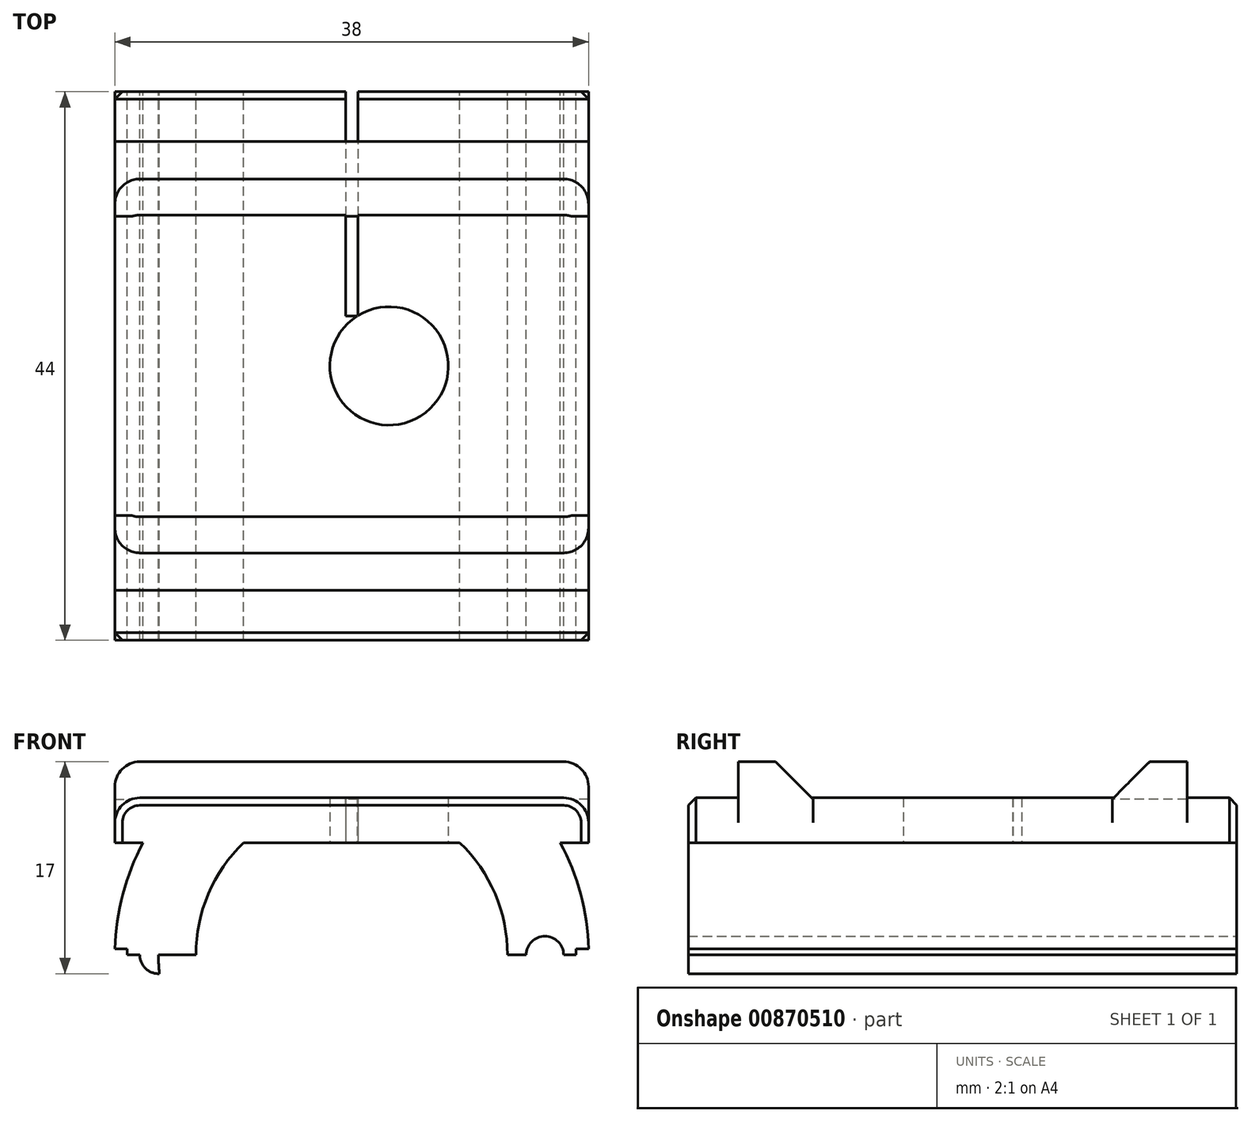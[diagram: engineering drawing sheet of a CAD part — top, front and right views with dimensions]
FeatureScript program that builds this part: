
annotation { "Feature Type Name" : "Feature", "Feature Type Description" : "" }
export const myFeature = defineFeature(function(context is Context, id is Id, definition is map)
    precondition{}
    {
        {
            var Q0;
            Q0=qCreatedBy(makeId("Top.planeOp"),FACE);
            var sketch = newSketch(context, id + "F0", { "sketchPlane" : qUnion([Q0])});
            skLineSegment(sketch, "E0.bottom", {"start": v(9.5, 19) * mm, "end": v(-9.5, 19) * mm});
            skLineSegment(sketch, "E0.top", {"start": v(9.5, -19) * mm, "end": v(-9.5, -19) * mm});
            skLineSegment(sketch, "E0.left", {"start": v(9.5, 19) * mm, "end": v(9.5, -19) * mm});
            skLineSegment(sketch, "E0.right", {"start": v(-9.5, 19) * mm, "end": v(-9.5, -19) * mm});
            skPoint(sketch, "E0.middle", {"position": v(0, 0) * mm});
            skLineSegment(sketch, "E1.bottom", {"start": v(-13.5, 22) * mm, "end": v(13.5, 22) * mm});
            skLineSegment(sketch, "E1.top", {"start": v(-13.5, -22) * mm, "end": v(13.5, -22) * mm});
            skLineSegment(sketch, "E1.left", {"start": v(-13.5, 22) * mm, "end": v(-13.5, -22) * mm});
            skLineSegment(sketch, "E1.right", {"start": v(13.5, 22) * mm, "end": v(13.5, -22) * mm});
            skCircle(sketch, "E2", {"center": v(3, 0) * mm, "radius": 4.75 * mm});
            skLineSegment(sketch, "E3.bottom", {"start": v(-0.5, 4) * mm, "end": v(0.5, 4) * mm});
            skLineSegment(sketch, "E3.top", {"start": v(-0.5, 29) * mm, "end": v(0.5, 29) * mm});
            skLineSegment(sketch, "E3.left", {"start": v(-0.5, 4) * mm, "end": v(-0.5, 29) * mm});
            skLineSegment(sketch, "E3.right", {"start": v(0.5, 4) * mm, "end": v(0.5, 29) * mm});
            skPoint(sketch, "E3.middle", {"position": v(0, 16.5) * mm});
            skPoint(sketch, "E3.middle.positionSnap0", {"position": v(0, 19) * mm});
            skPoint(sketch, "E3.centerSnap0", {"position": v(0, 19) * mm});
            skLineSegment(sketch, "E4.bottom", {"start": v(18.55, 25) * mm, "end": v(-18.55, 25) * mm});
            skLineSegment(sketch, "E4.top", {"start": v(18.55, -25) * mm, "end": v(-18.55, -25) * mm});
            skLineSegment(sketch, "E4.left", {"start": v(18.55, 25) * mm, "end": v(18.55, -25) * mm});
            skLineSegment(sketch, "E4.right", {"start": v(-18.55, 25) * mm, "end": v(-18.55, -25) * mm});
            skSolve(sketch);
        }
        {
            var Q0;
            Q0=qCreatedBy(makeId("Front.planeOp"),FACE);
            var sketch = newSketch(context, id + "F1", { "sketchPlane" : qUnion([Q0])});
            skCircle(sketch, "E5", {"center": v(0, 0) * mm, "radius": 9.5 * mm});
            skLineSegment(sketch, "E6.bottom", {"start": v(9.5, 6) * mm, "end": v(-9.5, 6) * mm});
            skLineSegment(sketch, "E6.top", {"start": v(9.5, -6) * mm, "end": v(-9.5, -6) * mm});
            skLineSegment(sketch, "E6.left", {"start": v(9.5, 6) * mm, "end": v(9.5, -6) * mm});
            skLineSegment(sketch, "E6.right", {"start": v(-9.5, 6) * mm, "end": v(-9.5, -6) * mm});
            skCircle(sketch, "E7", {"center": v(0, 0) * mm, "radius": 12.5 * mm});
            skLineSegment(sketch, "E8.bottom", {"start": v(-15.14, 9) * mm, "end": v(15.14, 9) * mm});
            skLineSegment(sketch, "E8.top", {"start": v(-15.14, -9) * mm, "end": v(15.14, -9) * mm});
            skLineSegment(sketch, "E8.left", {"start": v(-15.14, 9) * mm, "end": v(-15.14, -9) * mm});
            skLineSegment(sketch, "E8.right", {"start": v(15.14, 9) * mm, "end": v(15.14, -9) * mm});
            skLineSegment(sketch, "E9.bottom", {"start": v(-19, 12.6) * mm, "end": v(19, 12.6) * mm});
            skLineSegment(sketch, "E9.top", {"start": v(-19, -12.6) * mm, "end": v(19, -12.6) * mm});
            skLineSegment(sketch, "E9.left", {"start": v(-19, 12.6) * mm, "end": v(-19, -12.6) * mm});
            skLineSegment(sketch, "E9.right", {"start": v(19, 12.6) * mm, "end": v(19, -12.6) * mm});
            skCircle(sketch, "E10", {"center": v(0, 0) * mm, "radius": 15.5 * mm});
            skLineSegment(sketch, "E11", {"start": v(-15.14, 9) * mm, "end": v(-19, 9) * mm});
            skLineSegment(sketch, "E12", {"start": v(15.14, 9) * mm, "end": v(19, 9) * mm});
            skLineSegment(sketch, "E13", {"start": v(-15.14, -9) * mm, "end": v(-19, -9) * mm});
            skLineSegment(sketch, "E14", {"start": v(15.14, -9) * mm, "end": v(19, -9) * mm});
            skCircle(sketch, "E15", {"center": v(0, 0) * mm, "radius": 19 * mm});
            skLineSegment(sketch, "E16", {"start": v(-19, 0) * mm, "end": v(19, 0) * mm});
            skCircle(sketch, "E17", {"center": v(-15.5, 0) * mm, "radius": 1.5 * mm});
            skPoint(sketch, "E17.centerSnap0", {"position": v(-15.14, 0) * mm});
            skCircle(sketch, "E18", {"center": v(15.5, 0) * mm, "radius": 1.5 * mm});
            skLineSegment(sketch, "E19.bottom", {"start": v(-19, 0) * mm, "end": v(-18, 0) * mm});
            skLineSegment(sketch, "E19.top", {"start": v(-19, 0.5) * mm, "end": v(-18, 0.5) * mm});
            skLineSegment(sketch, "E19.left", {"start": v(-19, 0) * mm, "end": v(-19, 0.5) * mm});
            skLineSegment(sketch, "E19.right", {"start": v(-18, 0) * mm, "end": v(-18, 0.5) * mm});
            skLineSegment(sketch, "E20.bottom", {"start": v(19, 0) * mm, "end": v(18, 0) * mm});
            skLineSegment(sketch, "E20.top", {"start": v(19, 0.5) * mm, "end": v(18, 0.5) * mm});
            skLineSegment(sketch, "E20.left", {"start": v(19, 0) * mm, "end": v(19, 0.5) * mm});
            skLineSegment(sketch, "E20.right", {"start": v(18, 0) * mm, "end": v(18, 0.5) * mm});
            skSolve(sketch);
        }
        {
            var Q0;
            {var subQ7=sQuery(id+"F1.wireOp",EDGE,"E16");var subQ9=sQuery(id+"F1.wireOp",EDGE,"E7");var subQ11=makeQuery(id+"F1.imprint","INTERSECT",VERTEX,{"disambiguationData":[OD(0.0)],"derivedFrom":[subQ9,subQ7]});Q0=makeQuery(id+"F1.imprint","IMPRINT",FACE,{"disambiguationData":[TD([[makeQuery(id+"F1.imprint","IMPRINT",EDGE,{"disambiguationData":[TD([[subQ11,-1.0]])],"derivedFrom":subQ9}),-1.0]])]});}
            var Q1;
            {var subQ0=sQuery(id+"F1.wireOp",EDGE,"E8.bottom");var subQ1=sQuery(id+"F1.wireOp",EDGE,"E5");var subQ2=makeQuery(id+"F1.imprint","INTERSECT",VERTEX,{"disambiguationData":[OD(0.0)],"derivedFrom":[subQ1,subQ0]});Q1=makeQuery(id+"F1.imprint","IMPRINT",FACE,{"disambiguationData":[TD([[makeQuery(id+"F1.imprint","IMPRINT",EDGE,{"disambiguationData":[TD([[subQ2,1.0]])],"derivedFrom":subQ1}),-1.0]])]});}
            var Q2;
            {var subQ0=sQuery(id+"F1.wireOp",EDGE,"E10");var subQ1=sQuery(id+"F1.wireOp",EDGE,"E8.bottom");var subQ2=makeQuery(id+"F1.imprint","INTERSECT",VERTEX,{"disambiguationData":[OD(0.0)],"derivedFrom":[subQ1,subQ0]});Q2=makeQuery(id+"F1.imprint","IMPRINT",FACE,{"disambiguationData":[TD([[makeQuery(id+"F1.imprint","IMPRINT",EDGE,{"disambiguationData":[TD([[subQ2,-1.0]])],"derivedFrom":subQ0}),-1.0]])]});}
            var Q3;
            {var subQ1=sQuery(id+"F1.wireOp",EDGE,"E8.bottom");var subQ3=sQuery(id+"F1.wireOp",EDGE,"E10");var subQ4=makeQuery(id+"F1.imprint","INTERSECT",VERTEX,{"disambiguationData":[OD(1.0)],"derivedFrom":[subQ1,subQ3]});Q3=makeQuery(id+"F1.imprint","IMPRINT",FACE,{"disambiguationData":[TD([[makeQuery(id+"F1.imprint","IMPRINT",EDGE,{"disambiguationData":[TD([[subQ4,1.0]])],"derivedFrom":subQ3}),-1.0]])]});}
            var Q4;
            {var subQ0=sQuery(id+"F1.wireOp",EDGE,"E8.bottom");var subQ1=sQuery(id+"F1.wireOp",EDGE,"E7");var subQ2=makeQuery(id+"F1.imprint","INTERSECT",VERTEX,{"disambiguationData":[OD(0.0)],"derivedFrom":[subQ1,subQ0]});Q4=makeQuery(id+"F1.imprint","IMPRINT",FACE,{"disambiguationData":[TD([[makeQuery(id+"F1.imprint","IMPRINT",EDGE,{"disambiguationData":[TD([[subQ2,-1.0]])],"derivedFrom":subQ1}),-1.0]])]});}
            var Q5;
            {var subQ0=sQuery(id+"F1.wireOp",EDGE,"E8.bottom");var subQ1=sQuery(id+"F1.wireOp",EDGE,"E7");var subQ2=makeQuery(id+"F1.imprint","INTERSECT",VERTEX,{"disambiguationData":[OD(0.0)],"derivedFrom":[subQ1,subQ0]});Q5=makeQuery(id+"F1.imprint","IMPRINT",FACE,{"disambiguationData":[TD([[makeQuery(id+"F1.imprint","IMPRINT",EDGE,{"disambiguationData":[TD([[subQ2,-1.0]])],"derivedFrom":subQ1}),-1.0]])]});}
            var Q6;
            {var subQ0=sQuery(id+"F1.wireOp",EDGE,"E10");var subQ1=sQuery(id+"F1.wireOp",EDGE,"E8.left");var subQ2=makeQuery(id+"F1.imprint","INTERSECT",VERTEX,{"disambiguationData":[OD(0.0)],"derivedFrom":[subQ1,subQ0]});Q6=makeQuery(id+"F1.imprint","IMPRINT",FACE,{"disambiguationData":[TD([[makeQuery(id+"F1.imprint","IMPRINT",EDGE,{"disambiguationData":[TD([[subQ2,-1.0]])],"derivedFrom":subQ1}),-1.0]])]});}
            var Q7;
            {var subQ0=sQuery(id+"F1.wireOp",EDGE,"E10");var subQ1=sQuery(id+"F1.wireOp",EDGE,"E8.right");var subQ2=makeQuery(id+"F1.imprint","INTERSECT",VERTEX,{"disambiguationData":[OD(1.0)],"derivedFrom":[subQ1,subQ0]});Q7=makeQuery(id+"F1.imprint","IMPRINT",FACE,{"disambiguationData":[TD([[makeQuery(id+"F1.imprint","IMPRINT",EDGE,{"disambiguationData":[TD([[subQ2,-1.0]])],"derivedFrom":subQ1}),1.0]])]});}
            var Q8;
            {var subQ0=sQuery(id+"F1.wireOp",EDGE,"E15");var subQ1=sQuery(id+"F1.wireOp",EDGE,"E9.bottom");var subQ2=makeQuery(id+"F1.imprint","INTERSECT",VERTEX,{"disambiguationData":[OD(0.0)],"derivedFrom":[subQ1,subQ0]});Q8=makeQuery(id+"F1.imprint","IMPRINT",FACE,{"disambiguationData":[TD([[makeQuery(id+"F1.imprint","IMPRINT",EDGE,{"disambiguationData":[TD([[subQ2,1.0]])],"derivedFrom":subQ1}),-1.0]])]});}
            var Q9;
            {var subQ5=sQuery(id+"F1.wireOp",EDGE,"E10");var subQ7=sQuery(id+"F1.wireOp",EDGE,"E9.bottom");var subQ8=makeQuery(id+"F1.imprint","INTERSECT",VERTEX,{"disambiguationData":[OD(0.0)],"derivedFrom":[subQ7,subQ5]});Q9=makeQuery(id+"F1.imprint","IMPRINT",FACE,{"disambiguationData":[TD([[makeQuery(id+"F1.imprint","IMPRINT",EDGE,{"disambiguationData":[TD([[subQ8,1.0]])],"derivedFrom":subQ7}),-1.0]])]});}
            var Q10;
            {var subQ0=sQuery(id+"F1.wireOp",EDGE,"E15");var subQ7=sQuery(id+"F1.wireOp",EDGE,"E9.bottom");var subQ9=makeQuery(id+"F1.imprint","INTERSECT",VERTEX,{"disambiguationData":[OD(1.0)],"derivedFrom":[subQ7,subQ0]});Q10=makeQuery(id+"F1.imprint","IMPRINT",FACE,{"disambiguationData":[TD([[makeQuery(id+"F1.imprint","IMPRINT",EDGE,{"disambiguationData":[TD([[subQ9,1.0]])],"derivedFrom":subQ7}),-1.0]])]});}
            var Q11;
            {var subQ0=sQuery(id+"F1.wireOp",EDGE,"E9.right");var subQ1=sQuery(id+"F1.wireOp",EDGE,"E9.bottom");var subQ2=makeQuery(id+"F1.imprint","INTERSECT",VERTEX,{"derivedFrom":[subQ1,subQ0]});Q11=makeQuery(id+"F1.imprint","IMPRINT",FACE,{"disambiguationData":[TD([[makeQuery(id+"F1.imprint","IMPRINT",EDGE,{"disambiguationData":[TD([[subQ2,1.0]])],"derivedFrom":subQ1}),-1.0]])]});}
            var Q12;
            {var subQ11=sQuery(id+"F1.wireOp",EDGE,"E19.right");Q12=makeQuery(id+"F1.imprint","IMPRINT",FACE,{"disambiguationData":[TD([[makeQuery(id+"F1.imprint","IMPRINT",EDGE,{"derivedFrom":subQ11}),-1.0]])]});}
            var Q13;
            {var subQ11=sQuery(id+"F1.wireOp",EDGE,"E20.right");Q13=makeQuery(id+"F1.imprint","IMPRINT",FACE,{"disambiguationData":[TD([[makeQuery(id+"F1.imprint","IMPRINT",EDGE,{"derivedFrom":subQ11}),1.0]])]});}
            var Q14;
            {var subQ1=sQuery(id+"F1.wireOp",EDGE,"E8.bottom");var subQ7=sQuery(id+"F1.wireOp",EDGE,"E7");var subQ8=makeQuery(id+"F1.imprint","INTERSECT",VERTEX,{"disambiguationData":[OD(1.0)],"derivedFrom":[subQ7,subQ1]});Q14=makeQuery(id+"F1.imprint","IMPRINT",FACE,{"disambiguationData":[TD([[makeQuery(id+"F1.imprint","IMPRINT",EDGE,{"disambiguationData":[TD([[subQ8,-1.0]])],"derivedFrom":subQ7}),-1.0]])]});}
            var Q15;
            {var subQ0=sQuery(id+"F1.wireOp",EDGE,"E8.bottom");var subQ1=sQuery(id+"F1.wireOp",EDGE,"E5");var subQ2=makeQuery(id+"F1.imprint","INTERSECT",VERTEX,{"disambiguationData":[OD(0.0)],"derivedFrom":[subQ1,subQ0]});Q15=makeQuery(id+"F1.imprint","IMPRINT",FACE,{"disambiguationData":[TD([[makeQuery(id+"F1.imprint","IMPRINT",EDGE,{"disambiguationData":[TD([[subQ2,1.0]])],"derivedFrom":subQ1}),1.0]])]});}
            var Q16;
            {var subQ0=sQuery(id+"F1.wireOp",EDGE,"E17");var subQ1=sQuery(id+"F1.wireOp",EDGE,"E10");var subQ2=makeQuery(id+"F1.imprint","INTERSECT",VERTEX,{"disambiguationData":[OD(0.0)],"derivedFrom":[subQ1,subQ0]});Q16=makeQuery(id+"F1.imprint","IMPRINT",FACE,{"disambiguationData":[TD([[makeQuery(id+"F1.imprint","IMPRINT",EDGE,{"disambiguationData":[TD([[subQ2,-1.0]])],"derivedFrom":subQ1}),-1.0]])]});}
            var Q17;
            {var subQ0=sQuery(id+"F1.wireOp",EDGE,"E16");var subQ1=sQuery(id+"F1.wireOp",EDGE,"E10");var subQ2=makeQuery(id+"F1.imprint","INTERSECT",VERTEX,{"disambiguationData":[OD(1.0)],"derivedFrom":[subQ1,subQ0]});Q17=makeQuery(id+"F1.imprint","IMPRINT",FACE,{"disambiguationData":[TD([[makeQuery(id+"F1.imprint","IMPRINT",EDGE,{"disambiguationData":[TD([[subQ2,-1.0]])],"derivedFrom":subQ1}),-1.0]])]});}
            var Q18;
            {var subQ0=sQuery(id+"F1.wireOp",EDGE,"E17");var subQ1=sQuery(id+"F1.wireOp",EDGE,"E8.left");var subQ2=makeQuery(id+"F1.imprint","INTERSECT",VERTEX,{"disambiguationData":[OD(0.0)],"derivedFrom":[subQ1,subQ0]});Q18=makeQuery(id+"F1.imprint","IMPRINT",FACE,{"disambiguationData":[TD([[makeQuery(id+"F1.imprint","IMPRINT",EDGE,{"disambiguationData":[TD([[subQ2,1.0]])],"derivedFrom":subQ1}),1.0]])]});}
            var Q19;
            {var subQ0=sQuery(id+"F1.wireOp",EDGE,"E16");var subQ1=sQuery(id+"F1.wireOp",EDGE,"E8.left");var subQ2=makeQuery(id+"F1.imprint","INTERSECT",VERTEX,{"derivedFrom":[subQ1,subQ0]});Q19=makeQuery(id+"F1.imprint","IMPRINT",FACE,{"disambiguationData":[TD([[makeQuery(id+"F1.imprint","IMPRINT",EDGE,{"disambiguationData":[TD([[subQ2,1.0]])],"derivedFrom":subQ1}),1.0]])]});}
            var Q20;
            {var subQ0=sQuery(id+"F1.wireOp",EDGE,"E16");var subQ1=sQuery(id+"F1.wireOp",EDGE,"E8.left");var subQ2=makeQuery(id+"F1.imprint","INTERSECT",VERTEX,{"derivedFrom":[subQ1,subQ0]});Q20=makeQuery(id+"F1.imprint","IMPRINT",FACE,{"disambiguationData":[TD([[makeQuery(id+"F1.imprint","IMPRINT",EDGE,{"disambiguationData":[TD([[subQ2,1.0]])],"derivedFrom":subQ1}),-1.0]])]});}
            var Q21;
            {var subQ0=sQuery(id+"F1.wireOp",EDGE,"E17");var subQ1=sQuery(id+"F1.wireOp",EDGE,"E8.left");var subQ2=makeQuery(id+"F1.imprint","INTERSECT",VERTEX,{"disambiguationData":[OD(0.0)],"derivedFrom":[subQ1,subQ0]});Q21=makeQuery(id+"F1.imprint","IMPRINT",FACE,{"disambiguationData":[TD([[makeQuery(id+"F1.imprint","IMPRINT",EDGE,{"disambiguationData":[TD([[subQ2,1.0]])],"derivedFrom":subQ1}),-1.0]])]});}
            extrude(context, id + "F2", {"entities" : qUnion([Q0, Q1, Q2, Q3, Q4, Q5, Q6, Q7, Q8, Q9, Q10, Q11, Q12, Q13, Q14, Q15, Q16, Q17, Q18, Q19, Q20, Q21]), "endBound" : BoundingType.SYMMETRIC, "depth" : 44 * mm, "offsetDistance" : 25 * mm});
        }
        {
            var Q0;
            Q0=makeQuery(id+"F0.imprint","IMPRINT",FACE,{"disambiguationData":[TD([[makeQuery(id+"F0.imprint","IMPRINT",EDGE,{"derivedFrom":sQuery(id+"F0.wireOp",EDGE,"E2")}),1.0]])]});
            extrude(context, id + "F3", {"entities" : qUnion([Q0]), "operationType" : NewBodyOperationType.REMOVE, "depth" : 25 * mm, "offsetDistance" : 25 * mm});
        }
        {
            var Q0;
            {var subQ5=sQuery(id+"F0.wireOp",EDGE,"E3.bottom");Q0=makeQuery(id+"F0.imprint","IMPRINT",FACE,{"disambiguationData":[TD([[makeQuery(id+"F0.imprint","IMPRINT",EDGE,{"derivedFrom":subQ5}),1.0]])]});}
            var Q1;
            {var subQ0=sQuery(id+"F0.wireOp",EDGE,"E3.right");var subQ1=sQuery(id+"F0.wireOp",EDGE,"E0.bottom");var subQ2=makeQuery(id+"F0.imprint","INTERSECT",VERTEX,{"derivedFrom":[subQ1,subQ0]});Q1=makeQuery(id+"F0.imprint","IMPRINT",FACE,{"disambiguationData":[TD([[makeQuery(id+"F0.imprint","IMPRINT",EDGE,{"disambiguationData":[TD([[subQ2,-1.0]])],"derivedFrom":subQ1}),-1.0]])]});}
            var Q2;
            {var subQ5=sQuery(id+"F0.wireOp",EDGE,"E3.top");Q2=makeQuery(id+"F0.imprint","IMPRINT",FACE,{"disambiguationData":[TD([[makeQuery(id+"F0.imprint","IMPRINT",EDGE,{"derivedFrom":subQ5}),-1.0]])]});}
            var Q3;
            {var subQ5=sQuery(id+"F0.wireOp",EDGE,"E0.bottom");var subQ7=sQuery(id+"F0.wireOp",EDGE,"E3.right");var subQ9=makeQuery(id+"F0.imprint","INTERSECT",VERTEX,{"derivedFrom":[subQ5,subQ7]});Q3=makeQuery(id+"F0.imprint","IMPRINT",FACE,{"disambiguationData":[TD([[makeQuery(id+"F0.imprint","IMPRINT",EDGE,{"disambiguationData":[TD([[subQ9,-1.0]])],"derivedFrom":subQ5}),1.0]])]});}
            extrude(context, id + "F4", {"entities" : qUnion([Q0, Q1, Q2, Q3]), "operationType" : NewBodyOperationType.REMOVE, "depth" : 25 * mm, "offsetDistance" : 25 * mm});
        }
        {
            var Q0;
            Q0=qCreatedBy(makeId("Right.planeOp"),FACE);
            var sketch = newSketch(context, id + "F5", { "sketchPlane" : qUnion([Q0])});
            skLineSegment(sketch, "E21.bottom", {"start": v(22, -12.5) * mm, "end": v(-22, -12.5) * mm});
            skLineSegment(sketch, "E21.top", {"start": v(22, 12.5) * mm, "end": v(-22, 12.5) * mm});
            skLineSegment(sketch, "E21.left", {"start": v(22, -12.5) * mm, "end": v(22, 12.5) * mm});
            skLineSegment(sketch, "E21.right", {"start": v(-22, -12.5) * mm, "end": v(-22, 12.5) * mm});
            skPoint(sketch, "E21.middle", {"position": v(0, 0) * mm});
            skLineSegment(sketch, "E22.bottom", {"start": v(18, 12.5) * mm, "end": v(12, 12.5) * mm});
            skLineSegment(sketch, "E22.top", {"start": v(18, 15.5) * mm, "end": v(12, 15.5) * mm});
            skLineSegment(sketch, "E22.left", {"start": v(18, 12.5) * mm, "end": v(18, 15.5) * mm});
            skLineSegment(sketch, "E22.right", {"start": v(12, 12.5) * mm, "end": v(12, 15.5) * mm});
            skLineSegment(sketch, "E23.bottom", {"start": v(-18, 12.5) * mm, "end": v(-12, 12.5) * mm});
            skLineSegment(sketch, "E23.top", {"start": v(-18, 15.5) * mm, "end": v(-12, 15.5) * mm});
            skLineSegment(sketch, "E23.left", {"start": v(-18, 12.5) * mm, "end": v(-18, 15.5) * mm});
            skLineSegment(sketch, "E23.right", {"start": v(-12, 12.5) * mm, "end": v(-12, 15.5) * mm});
            skSolve(sketch);
        }
        {
            var Q0;
            Q0=makeQuery(id+"F5.imprint","IMPRINT",FACE,{"disambiguationData":[TD([[makeQuery(id+"F5.imprint","IMPRINT",EDGE,{"derivedFrom":sQuery(id+"F5.wireOp",EDGE,"E23.top")}),-1.0]])]});
            var Q1;
            Q1=makeQuery(id+"F5.imprint","IMPRINT",FACE,{"disambiguationData":[TD([[makeQuery(id+"F5.imprint","IMPRINT",EDGE,{"derivedFrom":sQuery(id+"F5.wireOp",EDGE,"E22.top")}),1.0]])]});
            extrude(context, id + "F6", {"entities" : qUnion([Q0, Q1]), "operationType" : NewBodyOperationType.ADD, "endBound" : BoundingType.SYMMETRIC, "depth" : 38 * mm, "offsetDistance" : 25 * mm});
        }
        {
            var Q0;
            {var subQ0=sQuery(id+"F5.wireOp",EDGE,"E23.left");var subQ2=sQuery(id+"F1.wireOp",EDGE,"E9.bottom");var subQ3=sQuery(id+"F1.wireOp",EDGE,"E9.right");Q0=makeQuery(id+"F6.boolean.opBoolean","SPLIT",EDGE,{"disambiguationData":[TD([makeQuery(id+"F6.opExtrude","SWEPT_FACE",FACE,{"disambiguationData":[OSD([subQ0])]})])],"derivedFrom":makeQuery(id+"F2.opExtrude","SWEPT_EDGE",EDGE,{"disambiguationData":[OSD([subQ2,subQ3])]})});}
            var Q1;
            Q1=makeQuery(id+"F6.opExtrude","CAP_EDGE",EDGE,{"disambiguationData":[OSD([sQuery(id+"F5.wireOp",EDGE,"E23.top")])],"isStart":false});
            var Q2;
            {var subQ2=sQuery(id+"F5.wireOp",EDGE,"E22.right");var subQ3=sQuery(id+"F1.wireOp",EDGE,"E9.right");var subQ4=sQuery(id+"F1.wireOp",EDGE,"E9.bottom");Q2=makeQuery(id+"F6.boolean.opBoolean","SPLIT",EDGE,{"disambiguationData":[TD([makeQuery(id+"F6.opExtrude","SWEPT_FACE",FACE,{"disambiguationData":[OSD([subQ2])]})])],"derivedFrom":makeQuery(id+"F2.opExtrude","SWEPT_EDGE",EDGE,{"disambiguationData":[OSD([subQ4,subQ3])]})});}
            var Q3;
            Q3=makeQuery(id+"F6.opExtrude","CAP_EDGE",EDGE,{"disambiguationData":[OSD([sQuery(id+"F5.wireOp",EDGE,"E22.top")])],"isStart":false});
            var Q4;
            {var subQ1=sQuery(id+"F1.wireOp",EDGE,"E9.right");var subQ2=sQuery(id+"F1.wireOp",EDGE,"E9.bottom");var subQ3=sQuery(id+"F5.wireOp",EDGE,"E22.left");Q4=makeQuery(id+"F6.boolean.opBoolean","SPLIT",EDGE,{"disambiguationData":[TD([makeQuery(id+"F6.opExtrude","SWEPT_FACE",FACE,{"disambiguationData":[OSD([subQ3])]})])],"derivedFrom":makeQuery(id+"F2.opExtrude","SWEPT_EDGE",EDGE,{"disambiguationData":[OSD([subQ2,subQ1])]})});}
            var Q5;
            {var subQ0=sQuery(id+"F5.wireOp",EDGE,"E23.left");var subQ2=sQuery(id+"F1.wireOp",EDGE,"E9.left");var subQ3=sQuery(id+"F1.wireOp",EDGE,"E9.bottom");Q5=makeQuery(id+"F6.boolean.opBoolean","SPLIT",EDGE,{"disambiguationData":[TD([makeQuery(id+"F6.opExtrude","SWEPT_FACE",FACE,{"disambiguationData":[OSD([subQ0])]})])],"derivedFrom":makeQuery(id+"F2.opExtrude","SWEPT_EDGE",EDGE,{"disambiguationData":[OSD([subQ3,subQ2])]})});}
            var Q6;
            Q6=makeQuery(id+"F6.opExtrude","CAP_EDGE",EDGE,{"disambiguationData":[OSD([sQuery(id+"F5.wireOp",EDGE,"E23.top")])],"isStart":true});
            var Q7;
            {var subQ2=sQuery(id+"F5.wireOp",EDGE,"E22.right");var subQ3=sQuery(id+"F1.wireOp",EDGE,"E9.left");var subQ4=sQuery(id+"F1.wireOp",EDGE,"E9.bottom");Q7=makeQuery(id+"F6.boolean.opBoolean","SPLIT",EDGE,{"disambiguationData":[TD([makeQuery(id+"F6.opExtrude","SWEPT_FACE",FACE,{"disambiguationData":[OSD([subQ2])]})])],"derivedFrom":makeQuery(id+"F2.opExtrude","SWEPT_EDGE",EDGE,{"disambiguationData":[OSD([subQ4,subQ3])]})});}
            var Q8;
            Q8=makeQuery(id+"F6.opExtrude","CAP_EDGE",EDGE,{"disambiguationData":[OSD([sQuery(id+"F5.wireOp",EDGE,"E22.top")])],"isStart":true});
            var Q9;
            {var subQ1=sQuery(id+"F1.wireOp",EDGE,"E9.bottom");var subQ2=sQuery(id+"F1.wireOp",EDGE,"E9.left");var subQ3=sQuery(id+"F5.wireOp",EDGE,"E22.left");Q9=makeQuery(id+"F6.boolean.opBoolean","SPLIT",EDGE,{"disambiguationData":[TD([makeQuery(id+"F6.opExtrude","SWEPT_FACE",FACE,{"disambiguationData":[OSD([subQ3])]})])],"derivedFrom":makeQuery(id+"F2.opExtrude","SWEPT_EDGE",EDGE,{"disambiguationData":[OSD([subQ1,subQ2])]})});}
            fillet(context, id + "F7", {"entities" : qUnion([Q0, Q1, Q2, Q3, Q4, Q5, Q6, Q7, Q8, Q9]), "radius" : 2 * mm, "tangentPropagation" : true, "allowEdgeOverflow" : false});
        }
        {
            var Q0;
            Q0=makeQuery(id+"F2.opExtrude","CAP_EDGE",EDGE,{"disambiguationData":[OSD([sQuery(id+"F1.wireOp",EDGE,"E9.bottom")])],"isStart":false});
            var Q1;
            {var subQ0=sQuery(id+"F1.wireOp",EDGE,"E9.right");var subQ1=sQuery(id+"F1.wireOp",EDGE,"E9.bottom");Q1=makeQuery(id+"F4.boolean.opBoolean","SPLIT",EDGE,{"disambiguationData":[TD([makeQuery(id+"F2.opExtrude","SWEPT_FACE",FACE,{"disambiguationData":[OSD([subQ0])]})])],"derivedFrom":makeQuery(id+"F2.opExtrude","CAP_EDGE",EDGE,{"disambiguationData":[OSD([subQ1])],"isStart":true})});}
            var Q2;
            {var subQ0=sQuery(id+"F1.wireOp",EDGE,"E9.left");var subQ1=sQuery(id+"F1.wireOp",EDGE,"E9.bottom");Q2=makeQuery(id+"F4.boolean.opBoolean","SPLIT",EDGE,{"disambiguationData":[TD([makeQuery(id+"F2.opExtrude","SWEPT_FACE",FACE,{"disambiguationData":[OSD([subQ0])]})])],"derivedFrom":makeQuery(id+"F2.opExtrude","CAP_EDGE",EDGE,{"disambiguationData":[OSD([subQ1])],"isStart":true})});}
            chamfer(context, id + "F8", {"entities" : qUnion([Q0, Q1, Q2]), "width" : 0.6 * mm, "tangentPropagation" : true});
        }
        {
            var Q0;
            Q0=makeQuery(id+"F6.opExtrude","SWEPT_EDGE",EDGE,{"disambiguationData":[OSD([sQuery(id+"F5.wireOp",EDGE,"E23.top"),sQuery(id+"F5.wireOp",EDGE,"E23.right")])]});
            var Q1;
            Q1=makeQuery(id+"F6.opExtrude","SWEPT_EDGE",EDGE,{"disambiguationData":[OSD([sQuery(id+"F5.wireOp",EDGE,"E22.top"),sQuery(id+"F5.wireOp",EDGE,"E22.right")])]});
            chamfer(context, id + "F9", {"entities" : qUnion([Q0, Q1]), "width" : 3 * mm});
        }
    });
